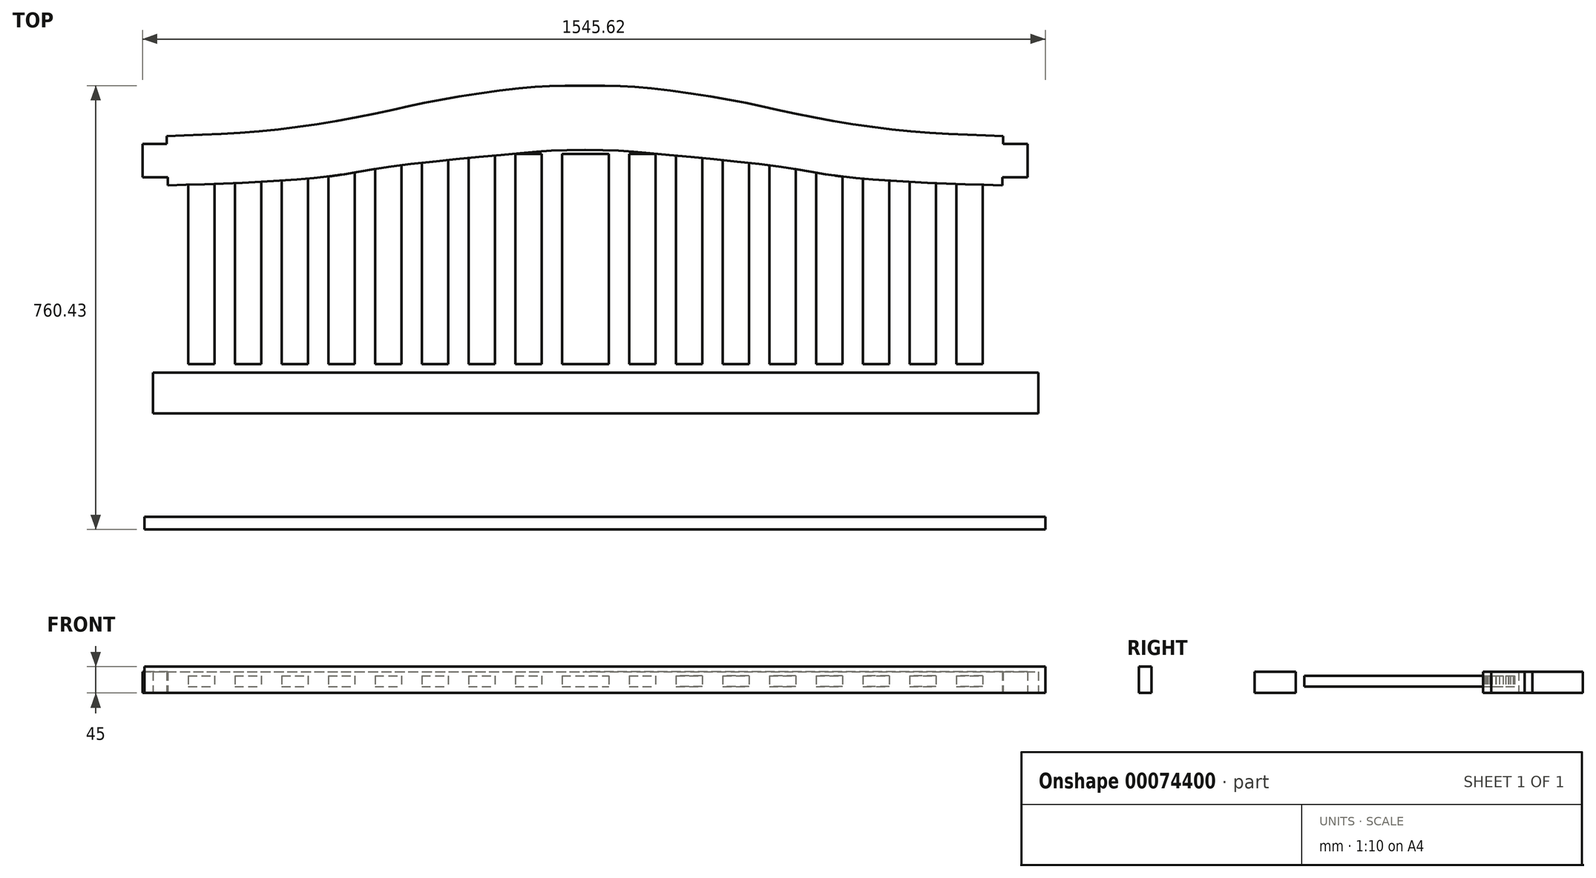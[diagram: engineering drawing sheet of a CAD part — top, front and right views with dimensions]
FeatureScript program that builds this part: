
annotation { "Feature Type Name" : "Feature", "Feature Type Description" : "" }
export const myFeature = defineFeature(function(context is Context, id is Id, definition is map)
    precondition{}
    {
        {
            var Q0;
            Q0=qCreatedBy(makeId("Top.planeOp"),FACE);
            var sketch = newSketch(context, id + "F0", { "sketchPlane" : qUnion([Q0])});
            skLineSegment(sketch, "E0", {"start": v(-321.5, -60.86) * mm, "end": v(-321.5, -46.73) * mm});
            skLineSegment(sketch, "E1", {"start": v(-321.5, -46.73) * mm, "end": v(-364.76, -46.73) * mm});
            skLineSegment(sketch, "E2", {"start": v(-364.76, -46.73) * mm, "end": v(-364.76, 10.25) * mm});
            skLineSegment(sketch, "E3", {"start": v(-364.76, 10.25) * mm, "end": v(-323.2, 10.25) * mm});
            skLineSegment(sketch, "E4", {"start": v(-323.2, 10.25) * mm, "end": v(-323.2, 23.58) * mm});
            skFitSpline(sketch, "E5", {"points": [v(-323.2, 23.58) * mm, v(-202.06, 29) * mm, v(-68.87, 43.5) * mm, v(63, 68.55) * mm, v(158.61, 88.34) * mm, v(294.93, 106.96) * mm, v(392.8, 110.03) * mm], "startDerivative": vector(667.25, 21.96) * mm, "endDerivative": vector(909.37, -3.45) * mm});
            skFitSpline(sketch, "E6", {"points": [v(-321.5, -60.86) * mm, v(-168.4, -55.14) * mm, v(-39.02, -44.57) * mm, v(67.92, -27.85) * mm, v(276.08, -6.15) * mm, v(392.8, 0) * mm], "startDerivative": vector(707.42, 21.81) * mm, "endDerivative": vector(775.37, 0) * mm});
            skLineSegment(sketch, "E7", {"start": v(-321.5, -60.86) * mm, "end": v(371.84, -60.86) * mm, "construction": true});
            skLineSegment(sketch, "E8", {"start": v(392.8, 0) * mm, "end": v(392.8, 110.03) * mm});
            skSolve(sketch);
        }
        {
            var Q0;
            Q0 = qSketchRegion(id + "F0", true);
            var Q1;
            Q1=makeQuery(id+"F0.imprint","IMPRINT",FACE,{"disambiguationData":[TD([[makeQuery(id+"F0.imprint","IMPRINT",EDGE,{"derivedFrom":sQuery(id+"F0.wireOp",EDGE,"E0")}),-1.0]])]});
            extrude(context, id + "F1", {"entities" : qUnion([Q0, Q1]), "depth" : 36 * mm});
        }
        {
            var Q0;
            Q0=makeQuery(id+"F1.opExtrude","SWEPT_FACE",FACE,{"disambiguationData":[OSD([sQuery(id+"F0.wireOp",EDGE,"E1")])]});
            cPlane(context, id + "F2", {"entities" : qUnion([Q0]), "cplaneType" : CPlaneType.OFFSET, "offset" : 20 * mm, "width" : 150 * mm, "height" : 150 * mm});
        }
        {
            var Q0;
            Q0=qCreatedBy(id+"F2.planeOp",FACE);
            var sketch = newSketch(context, id + "F3", { "sketchPlane" : qUnion([Q0])});
            skLineSegment(sketch, "E9.bottom", {"start": v(-286.5, 29.6) * mm, "end": v(-241.5, 29.6) * mm});
            skLineSegment(sketch, "E9.top", {"start": v(-286.5, 10.6) * mm, "end": v(-241.5, 10.6) * mm});
            skLineSegment(sketch, "E9.left", {"start": v(-286.5, 29.6) * mm, "end": v(-286.5, 10.6) * mm});
            skLineSegment(sketch, "E9.right", {"start": v(-241.5, 29.6) * mm, "end": v(-241.5, 10.6) * mm});
            skLineSegment(sketch, "E10.1.0.0", {"start": v(-206.5, 29.6) * mm, "end": v(-161.5, 29.6) * mm});
            skLineSegment(sketch, "E10.1.0.1", {"start": v(-206.5, 10.6) * mm, "end": v(-161.5, 10.6) * mm});
            skLineSegment(sketch, "E10.1.0.2", {"start": v(-161.5, 29.6) * mm, "end": v(-161.5, 10.6) * mm});
            skLineSegment(sketch, "E10.1.0.3", {"start": v(-206.5, 29.6) * mm, "end": v(-206.5, 10.6) * mm});
            skLineSegment(sketch, "E10.2.0.0", {"start": v(-126.5, 29.6) * mm, "end": v(-81.5, 29.6) * mm});
            skLineSegment(sketch, "E10.2.0.1", {"start": v(-126.5, 10.6) * mm, "end": v(-81.5, 10.6) * mm});
            skLineSegment(sketch, "E10.2.0.2", {"start": v(-81.5, 29.6) * mm, "end": v(-81.5, 10.6) * mm});
            skLineSegment(sketch, "E10.2.0.3", {"start": v(-126.5, 29.6) * mm, "end": v(-126.5, 10.6) * mm});
            skLineSegment(sketch, "E10.3.0.0", {"start": v(-46.5, 29.6) * mm, "end": v(-1.5, 29.6) * mm});
            skLineSegment(sketch, "E10.3.0.1", {"start": v(-46.5, 10.6) * mm, "end": v(-1.5, 10.6) * mm});
            skLineSegment(sketch, "E10.3.0.2", {"start": v(-1.5, 29.6) * mm, "end": v(-1.5, 10.6) * mm});
            skLineSegment(sketch, "E10.3.0.3", {"start": v(-46.5, 29.6) * mm, "end": v(-46.5, 10.6) * mm});
            skLineSegment(sketch, "E10.4.0.0", {"start": v(33.5, 29.6) * mm, "end": v(78.5, 29.6) * mm});
            skLineSegment(sketch, "E10.4.0.1", {"start": v(33.5, 10.6) * mm, "end": v(78.5, 10.6) * mm});
            skLineSegment(sketch, "E10.4.0.2", {"start": v(78.5, 29.6) * mm, "end": v(78.5, 10.6) * mm});
            skLineSegment(sketch, "E10.4.0.3", {"start": v(33.5, 29.6) * mm, "end": v(33.5, 10.6) * mm});
            skLineSegment(sketch, "E10.5.0.0", {"start": v(113.5, 29.6) * mm, "end": v(158.5, 29.6) * mm});
            skLineSegment(sketch, "E10.5.0.1", {"start": v(113.5, 10.6) * mm, "end": v(158.5, 10.6) * mm});
            skLineSegment(sketch, "E10.5.0.2", {"start": v(158.5, 29.6) * mm, "end": v(158.5, 10.6) * mm});
            skLineSegment(sketch, "E10.5.0.3", {"start": v(113.5, 29.6) * mm, "end": v(113.5, 10.6) * mm});
            skLineSegment(sketch, "E10.6.0.0", {"start": v(193.5, 29.6) * mm, "end": v(238.5, 29.6) * mm});
            skLineSegment(sketch, "E10.6.0.1", {"start": v(193.5, 10.6) * mm, "end": v(238.5, 10.6) * mm});
            skLineSegment(sketch, "E10.6.0.2", {"start": v(238.5, 29.6) * mm, "end": v(238.5, 10.6) * mm});
            skLineSegment(sketch, "E10.6.0.3", {"start": v(193.5, 29.6) * mm, "end": v(193.5, 10.6) * mm});
            skLineSegment(sketch, "E10.7.0.0", {"start": v(273.5, 29.6) * mm, "end": v(318.5, 29.6) * mm});
            skLineSegment(sketch, "E10.7.0.1", {"start": v(273.5, 10.6) * mm, "end": v(318.5, 10.6) * mm});
            skLineSegment(sketch, "E10.7.0.2", {"start": v(318.5, 29.6) * mm, "end": v(318.5, 10.6) * mm});
            skLineSegment(sketch, "E10.7.0.3", {"start": v(273.5, 29.6) * mm, "end": v(273.5, 10.6) * mm});
            skLineSegment(sketch, "E10.direction1", {"start": v(-286.5, 29.6) * mm, "end": v(-206.5, 29.6) * mm, "construction": true});
            skLineSegment(sketch, "E11.0.8.0", {"start": v(353.5, 29.6) * mm, "end": v(398.5, 29.6) * mm});
            skLineSegment(sketch, "E11.3.8.0", {"start": v(353.5, 10.6) * mm, "end": v(398.5, 10.6) * mm});
            skLineSegment(sketch, "E11.6.8.0", {"start": v(398.5, 29.6) * mm, "end": v(398.5, 10.6) * mm});
            skLineSegment(sketch, "E11.9.8.0", {"start": v(353.5, 29.6) * mm, "end": v(353.5, 10.6) * mm});
            skLineSegment(sketch, "E12.bottom", {"start": v(398.5, 29.6) * mm, "end": v(433.5, 29.6) * mm});
            skLineSegment(sketch, "E12.top", {"start": v(398.5, 10.6) * mm, "end": v(433.5, 10.6) * mm});
            skLineSegment(sketch, "E12.right", {"start": v(433.5, 29.6) * mm, "end": v(433.5, 10.6) * mm});
            skLineSegment(sketch, "E13.bottom", {"start": v(468.5, 29.6) * mm, "end": v(513.5, 29.6) * mm});
            skLineSegment(sketch, "E13.top", {"start": v(468.5, 10.6) * mm, "end": v(513.5, 10.6) * mm});
            skLineSegment(sketch, "E13.left", {"start": v(468.5, 29.6) * mm, "end": v(468.5, 10.6) * mm});
            skLineSegment(sketch, "E13.right", {"start": v(513.5, 29.6) * mm, "end": v(513.5, 10.6) * mm});
            skLineSegment(sketch, "E14.1.0.0", {"start": v(548.5, 29.6) * mm, "end": v(548.5, 10.6) * mm});
            skLineSegment(sketch, "E14.1.0.1", {"start": v(548.5, 29.6) * mm, "end": v(593.5, 29.6) * mm});
            skLineSegment(sketch, "E14.1.0.2", {"start": v(548.5, 10.6) * mm, "end": v(593.5, 10.6) * mm});
            skLineSegment(sketch, "E14.1.0.3", {"start": v(593.5, 29.6) * mm, "end": v(593.5, 10.6) * mm});
            skLineSegment(sketch, "E14.2.0.0", {"start": v(628.5, 29.6) * mm, "end": v(628.5, 10.6) * mm});
            skLineSegment(sketch, "E14.2.0.1", {"start": v(628.5, 29.6) * mm, "end": v(673.5, 29.6) * mm});
            skLineSegment(sketch, "E14.2.0.2", {"start": v(628.5, 10.6) * mm, "end": v(673.5, 10.6) * mm});
            skLineSegment(sketch, "E14.2.0.3", {"start": v(673.5, 29.6) * mm, "end": v(673.5, 10.6) * mm});
            skLineSegment(sketch, "E14.3.0.0", {"start": v(708.5, 29.6) * mm, "end": v(708.5, 10.6) * mm});
            skLineSegment(sketch, "E14.3.0.1", {"start": v(708.5, 29.6) * mm, "end": v(753.5, 29.6) * mm});
            skLineSegment(sketch, "E14.3.0.2", {"start": v(708.5, 10.6) * mm, "end": v(753.5, 10.6) * mm});
            skLineSegment(sketch, "E14.3.0.3", {"start": v(753.5, 29.6) * mm, "end": v(753.5, 10.6) * mm});
            skLineSegment(sketch, "E14.4.0.0", {"start": v(788.5, 29.6) * mm, "end": v(788.5, 10.6) * mm});
            skLineSegment(sketch, "E14.4.0.1", {"start": v(788.5, 29.6) * mm, "end": v(833.5, 29.6) * mm});
            skLineSegment(sketch, "E14.4.0.2", {"start": v(788.5, 10.6) * mm, "end": v(833.5, 10.6) * mm});
            skLineSegment(sketch, "E14.4.0.3", {"start": v(833.5, 29.6) * mm, "end": v(833.5, 10.6) * mm});
            skLineSegment(sketch, "E14.5.0.0", {"start": v(868.5, 29.6) * mm, "end": v(868.5, 10.6) * mm});
            skLineSegment(sketch, "E14.5.0.1", {"start": v(868.5, 29.6) * mm, "end": v(913.5, 29.6) * mm});
            skLineSegment(sketch, "E14.5.0.2", {"start": v(868.5, 10.6) * mm, "end": v(913.5, 10.6) * mm});
            skLineSegment(sketch, "E14.5.0.3", {"start": v(913.5, 29.6) * mm, "end": v(913.5, 10.6) * mm});
            skLineSegment(sketch, "E14.6.0.0", {"start": v(948.5, 29.6) * mm, "end": v(948.5, 10.6) * mm});
            skLineSegment(sketch, "E14.6.0.1", {"start": v(948.5, 29.6) * mm, "end": v(993.5, 29.6) * mm});
            skLineSegment(sketch, "E14.6.0.2", {"start": v(948.5, 10.6) * mm, "end": v(993.5, 10.6) * mm});
            skLineSegment(sketch, "E14.6.0.3", {"start": v(993.5, 29.6) * mm, "end": v(993.5, 10.6) * mm});
            skLineSegment(sketch, "E14.7.0.0", {"start": v(1028.5, 29.6) * mm, "end": v(1028.5, 10.6) * mm});
            skLineSegment(sketch, "E14.7.0.1", {"start": v(1028.5, 29.6) * mm, "end": v(1073.5, 29.6) * mm});
            skLineSegment(sketch, "E14.7.0.2", {"start": v(1028.5, 10.6) * mm, "end": v(1073.5, 10.6) * mm});
            skLineSegment(sketch, "E14.7.0.3", {"start": v(1073.5, 29.6) * mm, "end": v(1073.5, 10.6) * mm});
            skLineSegment(sketch, "E14.direction1", {"start": v(468.5, 10.6) * mm, "end": v(548.5, 10.6) * mm, "construction": true});
            skSolve(sketch);
        }
        {
            var Q0;
            Q0=makeQuery(id+"F1.opExtrude","SWEPT_FACE",FACE,{"disambiguationData":[OSD([sQuery(id+"F0.wireOp",EDGE,"E8")])]});
            cPlane(context, id + "F4", {"entities" : qUnion([Q0]), "cplaneType" : CPlaneType.OFFSET, "offset" : 0 * mm, "width" : 152.4 * mm, "height" : 152.4 * mm});
        }
        {
            var Q0;
            Q0=makeQuery(id+"F1.opExtrude","SWEPT_BODY",BODY,{"disambiguationData":[OSD([sQuery(id+"F0.wireOp",EDGE,"E0"),sQuery(id+"F0.wireOp",EDGE,"E1"),sQuery(id+"F0.wireOp",EDGE,"E2"),sQuery(id+"F0.wireOp",EDGE,"E3"),sQuery(id+"F0.wireOp",EDGE,"E4"),sQuery(id+"F0.wireOp",EDGE,"E5"),sQuery(id+"F0.wireOp",EDGE,"E6"),sQuery(id+"F0.wireOp",EDGE,"fr2kpR4b-QZiE-MCPt-JJRl-KWky7yjQkA4g")])]});
            var Q1;
            Q1=qCreatedBy(id+"F4.planeOp",FACE);
            mirror(context, id + "F5", {"operationType" : NewBodyOperationType.ADD, "entities" : qUnion([Q0]), "mirrorPlane" : qUnion([Q1])});
        }
        {
            var Q0;
            Q0=makeQuery(id+"F3.imprint","IMPRINT",FACE,{"disambiguationData":[TD([[makeQuery(id+"F3.imprint","IMPRINT",EDGE,{"derivedFrom":sQuery(id+"F3.wireOp",EDGE,"E10.1.0.0")}),-1.0]])]});
            var Q1;
            Q1=makeQuery(id+"F3.imprint","IMPRINT",FACE,{"disambiguationData":[TD([[makeQuery(id+"F3.imprint","IMPRINT",EDGE,{"derivedFrom":sQuery(id+"F3.wireOp",EDGE,"E10.2.0.0")}),-1.0]])]});
            var Q2;
            Q2=makeQuery(id+"F3.imprint","IMPRINT",FACE,{"disambiguationData":[TD([[makeQuery(id+"F3.imprint","IMPRINT",EDGE,{"derivedFrom":sQuery(id+"F3.wireOp",EDGE,"E10.3.0.0")}),-1.0]])]});
            var Q3;
            Q3=makeQuery(id+"F3.imprint","IMPRINT",FACE,{"disambiguationData":[TD([[makeQuery(id+"F3.imprint","IMPRINT",EDGE,{"derivedFrom":sQuery(id+"F3.wireOp",EDGE,"E10.4.0.0")}),-1.0]])]});
            var Q4;
            Q4=makeQuery(id+"F3.imprint","IMPRINT",FACE,{"disambiguationData":[TD([[makeQuery(id+"F3.imprint","IMPRINT",EDGE,{"derivedFrom":sQuery(id+"F3.wireOp",EDGE,"E10.5.0.0")}),-1.0]])]});
            var Q5;
            Q5=makeQuery(id+"F3.imprint","IMPRINT",FACE,{"disambiguationData":[TD([[makeQuery(id+"F3.imprint","IMPRINT",EDGE,{"derivedFrom":sQuery(id+"F3.wireOp",EDGE,"E10.6.0.0")}),-1.0]])]});
            var Q6;
            Q6=makeQuery(id+"F3.imprint","IMPRINT",FACE,{"disambiguationData":[TD([[makeQuery(id+"F3.imprint","IMPRINT",EDGE,{"derivedFrom":sQuery(id+"F3.wireOp",EDGE,"E10.7.0.0")}),-1.0]])]});
            var Q7;
            Q7=makeQuery(id+"F3.imprint","IMPRINT",FACE,{"disambiguationData":[TD([[makeQuery(id+"F3.imprint","IMPRINT",EDGE,{"derivedFrom":sQuery(id+"F3.wireOp",EDGE,"E13.bottom")}),-1.0]])]});
            var Q8;
            Q8=makeQuery(id+"F3.imprint","IMPRINT",FACE,{"disambiguationData":[TD([[makeQuery(id+"F3.imprint","IMPRINT",EDGE,{"derivedFrom":sQuery(id+"F3.wireOp",EDGE,"E14.1.0.0")}),1.0]])]});
            var Q9;
            Q9=makeQuery(id+"F3.imprint","IMPRINT",FACE,{"disambiguationData":[TD([[makeQuery(id+"F3.imprint","IMPRINT",EDGE,{"derivedFrom":sQuery(id+"F3.wireOp",EDGE,"E14.2.0.0")}),1.0]])]});
            var Q10;
            Q10=makeQuery(id+"F3.imprint","IMPRINT",FACE,{"disambiguationData":[TD([[makeQuery(id+"F3.imprint","IMPRINT",EDGE,{"derivedFrom":sQuery(id+"F3.wireOp",EDGE,"E14.3.0.0")}),1.0]])]});
            var Q11;
            Q11=makeQuery(id+"F3.imprint","IMPRINT",FACE,{"disambiguationData":[TD([[makeQuery(id+"F3.imprint","IMPRINT",EDGE,{"derivedFrom":sQuery(id+"F3.wireOp",EDGE,"E14.4.0.0")}),1.0]])]});
            var Q12;
            Q12=makeQuery(id+"F3.imprint","IMPRINT",FACE,{"disambiguationData":[TD([[makeQuery(id+"F3.imprint","IMPRINT",EDGE,{"derivedFrom":sQuery(id+"F3.wireOp",EDGE,"E14.5.0.0")}),1.0]])]});
            var Q13;
            Q13=makeQuery(id+"F3.imprint","IMPRINT",FACE,{"disambiguationData":[TD([[makeQuery(id+"F3.imprint","IMPRINT",EDGE,{"derivedFrom":sQuery(id+"F3.wireOp",EDGE,"E14.6.0.0")}),1.0]])]});
            var Q14;
            Q14=makeQuery(id+"F3.imprint","IMPRINT",FACE,{"disambiguationData":[TD([[makeQuery(id+"F3.imprint","IMPRINT",EDGE,{"derivedFrom":sQuery(id+"F3.wireOp",EDGE,"E14.7.0.0")}),1.0]])]});
            var Q15;
            Q15=makeQuery(id+"F3.imprint","IMPRINT",FACE,{"disambiguationData":[TD([[makeQuery(id+"F3.imprint","IMPRINT",EDGE,{"derivedFrom":sQuery(id+"F3.wireOp",EDGE,"E11.0.8.0")}),-1.0]])]});
            var Q16;
            Q16=makeQuery(id+"F3.imprint","IMPRINT",FACE,{"disambiguationData":[TD([[makeQuery(id+"F3.imprint","IMPRINT",EDGE,{"derivedFrom":sQuery(id+"F3.wireOp",EDGE,"E12.bottom")}),-1.0]])]});
            var Q17;
            Q17=makeQuery(id+"F3.imprint","IMPRINT",FACE,{"disambiguationData":[TD([[makeQuery(id+"F3.imprint","IMPRINT",EDGE,{"derivedFrom":sQuery(id+"F3.wireOp",EDGE,"E9.bottom")}),-1.0]])]});
            extrude(context, id + "F6", {"entities" : qUnion([Q0, Q1, Q2, Q3, Q4, Q5, Q6, Q7, Q8, Q9, Q10, Q11, Q12, Q13, Q14, Q15, Q16, Q17]), "operationType" : NewBodyOperationType.ADD, "depth" : 300 * mm, "hasSecondDirection" : true, "secondDirectionOppositeDirection" : true, "secondDirectionDepth" : 60 * mm});
        }
        {
            var Q0;
            Q0=qCreatedBy(makeId("Top.planeOp"),FACE);
            var sketch = newSketch(context, id + "F7", { "sketchPlane" : qUnion([Q0])});
            skLineSegment(sketch, "E15.bottom", {"start": v(-346.7, -381.76) * mm, "end": v(1168.9, -381.76) * mm});
            skLineSegment(sketch, "E15.top", {"start": v(-346.7, -451.76) * mm, "end": v(1168.9, -451.76) * mm});
            skLineSegment(sketch, "E15.left", {"start": v(-346.7, -381.76) * mm, "end": v(-346.7, -451.76) * mm});
            skLineSegment(sketch, "E15.right", {"start": v(1168.9, -381.76) * mm, "end": v(1168.9, -451.76) * mm});
            skSolve(sketch);
        }
        {
            var Q0;
            Q0=makeQuery(id+"F7.imprint","IMPRINT",FACE,{"disambiguationData":[TD([[makeQuery(id+"F7.imprint","IMPRINT",EDGE,{"derivedFrom":sQuery(id+"F7.wireOp",EDGE,"E15.bottom")}),-1.0]])]});
            extrude(context, id + "F8", {"entities" : qUnion([Q0]), "depth" : 36 * mm});
        }
        {
            var Q0;
            Q0=qCreatedBy(makeId("Top.planeOp"),FACE);
            var sketch = newSketch(context, id + "F9", { "sketchPlane" : qUnion([Q0])});
            skLineSegment(sketch, "E16.bottom", {"start": v(-361.14, -628.35) * mm, "end": v(1180.86, -628.35) * mm});
            skLineSegment(sketch, "E16.top", {"start": v(-361.14, -650.35) * mm, "end": v(1180.86, -650.35) * mm});
            skLineSegment(sketch, "E16.left", {"start": v(-361.14, -628.35) * mm, "end": v(-361.14, -650.35) * mm});
            skLineSegment(sketch, "E16.right", {"start": v(1180.86, -628.35) * mm, "end": v(1180.86, -650.35) * mm});
            skSolve(sketch);
        }
        {
            var Q0;
            Q0=makeQuery(id+"F9.imprint","IMPRINT",FACE,{"disambiguationData":[TD([[makeQuery(id+"F9.imprint","IMPRINT",EDGE,{"derivedFrom":sQuery(id+"F9.wireOp",EDGE,"E16.bottom")}),-1.0]])]});
            extrude(context, id + "F10", {"entities" : qUnion([Q0]), "depth" : 45 * mm});
        }
    });
